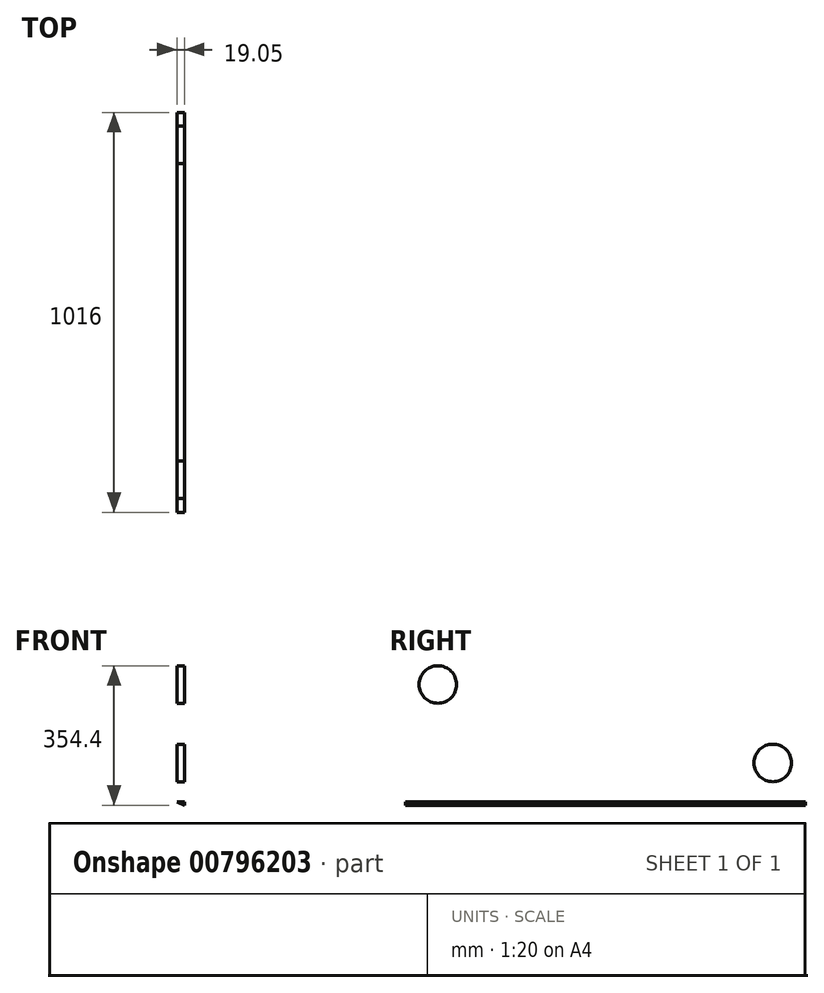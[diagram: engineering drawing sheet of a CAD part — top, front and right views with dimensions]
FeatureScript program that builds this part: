
annotation { "Feature Type Name" : "Feature", "Feature Type Description" : "" }
export const myFeature = defineFeature(function(context is Context, id is Id, definition is map)
    precondition{}
    {
        {
            var Q0;
            Q0=qCreatedBy(makeId("Front.planeOp"),FACE);
            var sketch = newSketch(context, id + "F0", { "sketchPlane" : qUnion([Q0])});
            skLineSegment(sketch, "E0", {"start": v(0, 0) * mm, "end": v(0, 406.4) * mm});
            skLineSegment(sketch, "E1", {"start": v(0, 406.4) * mm, "end": v(-19.05, 406.4) * mm});
            skLineSegment(sketch, "E2", {"start": v(-19.05, 406.4) * mm, "end": v(-19.05, 7.9) * mm});
            skLineSegment(sketch, "E3", {"start": v(0, 0) * mm, "end": v(-19.05, 7.9) * mm});
            skPoint(sketch, "E4.orphan", {"position": v(-19.05, 0) * mm});
            skSolve(sketch);
        }
        {
            var Q0;
            Q0=makeQuery(id+"F0.imprint","IMPRINT",FACE,{"disambiguationData":[TD([[makeQuery(id+"F0.imprint","IMPRINT",EDGE,{"derivedFrom":sQuery(id+"F0.wireOp",EDGE,"E0")}),1.0]])]});
            extrude(context, id + "F1", {"entities" : qUnion([Q0]), "depth" : 1016 * mm, "offsetDistance" : 25.4 * mm});
        }
        {
            var Q0;
            Q0=makeQuery(id+"F1.opExtrude","SWEPT_FACE",FACE,{"disambiguationData":[OSD([sQuery(id+"F0.wireOp",EDGE,"E2")])]});
            var sketch = newSketch(context, id + "F2", { "sketchPlane" : qUnion([Q0])});
            skLineSegment(sketch, "E5", {"start": v(0, 207.15) * mm, "end": v(165.1, 207.15) * mm, "construction": true});
            skLineSegment(sketch, "E6", {"start": v(165.1, 207.15) * mm, "end": v(165.1, 390.79) * mm, "construction": true});
            skLineSegment(sketch, "E7.bottom", {"start": v(165.1, 390.79) * mm, "end": v(850.9, 390.79) * mm});
            skLineSegment(sketch, "E7.top", {"start": v(165.1, 23.5) * mm, "end": v(850.9, 23.5) * mm});
            skLineSegment(sketch, "E7.left", {"start": v(165.1, 390.79) * mm, "end": v(165.1, 23.5) * mm});
            skLineSegment(sketch, "E7.right", {"start": v(850.9, 390.79) * mm, "end": v(850.9, 23.5) * mm});
            skSolve(sketch);
        }
        {
            var Q0;
            Q0=makeQuery(id+"F2.imprint","IMPRINT",FACE,{"disambiguationData":[TD([[makeQuery(id+"F2.imprint","IMPRINT",EDGE,{"derivedFrom":sQuery(id+"F2.wireOp",EDGE,"E7.bottom")}),-1.0]])]});
            extrude(context, id + "F3", {"entities" : qUnion([Q0]), "operationType" : NewBodyOperationType.REMOVE, "endBound" : BoundingType.THROUGH_ALL, "oppositeDirection" : true, "depth" : 25.4 * mm, "offsetDistance" : 25.4 * mm});
        }
        {
            var Q0;
            Q0=makeQuery(id+"F1.opExtrude","SWEPT_FACE",FACE,{"disambiguationData":[OSD([sQuery(id+"F0.wireOp",EDGE,"E2")])]});
            var sketch = newSketch(context, id + "F4", { "sketchPlane" : qUnion([Q0])});
            skLineSegment(sketch, "E8", {"start": v(165.1, 207.15) * mm, "end": v(0, 207.15) * mm, "construction": true});
            skLineSegment(sketch, "E9", {"start": v(82.55, 207.15) * mm, "end": v(82.55, 406.4) * mm, "construction": true});
            skCircle(sketch, "E10", {"center": v(82.55, 306.77) * mm, "radius": 47.63 * mm});
            skLineSegment(sketch, "E11", {"start": v(508, 23.5) * mm, "end": v(508, 390.79) * mm, "construction": true});
            skCircle(sketch, "E12.MirrorC", {"center": v(933.45, 306.77) * mm, "radius": 47.63 * mm});
            skCircle(sketch, "E13.MirrorC", {"center": v(82.55, 107.52) * mm, "radius": 47.63 * mm});
            skCircle(sketch, "E14.MirrorC", {"center": v(933.45, 107.52) * mm, "radius": 47.63 * mm});
            skSolve(sketch);
        }
        {
            var Q0;
            Q0=makeQuery(id+"F4.imprint","IMPRINT",FACE,{"disambiguationData":[TD([[makeQuery(id+"F4.imprint","IMPRINT",EDGE,{"derivedFrom":sQuery(id+"F4.wireOp",EDGE,"E10")}),1.0]])]});
            var Q1;
            Q1=makeQuery(id+"F4.imprint","IMPRINT",FACE,{"disambiguationData":[TD([[makeQuery(id+"F4.imprint","IMPRINT",EDGE,{"derivedFrom":sQuery(id+"F4.wireOp",EDGE,"E13.MirrorC")}),-1.0]])]});
            var Q2;
            Q2=makeQuery(id+"F4.imprint","IMPRINT",FACE,{"disambiguationData":[TD([[makeQuery(id+"F4.imprint","IMPRINT",EDGE,{"derivedFrom":sQuery(id+"F4.wireOp",EDGE,"E12.MirrorC")}),-1.0]])]});
            var Q3;
            Q3=makeQuery(id+"F4.imprint","IMPRINT",FACE,{"disambiguationData":[TD([[makeQuery(id+"F4.imprint","IMPRINT",EDGE,{"derivedFrom":sQuery(id+"F4.wireOp",EDGE,"E14.MirrorC")}),1.0]])]});
            extrude(context, id + "F5", {"entities" : qUnion([Q0, Q1, Q2, Q3]), "operationType" : NewBodyOperationType.REMOVE, "endBound" : BoundingType.THROUGH_ALL, "oppositeDirection" : true, "depth" : 25.4 * mm, "offsetDistance" : 25.4 * mm});
        }
    });
